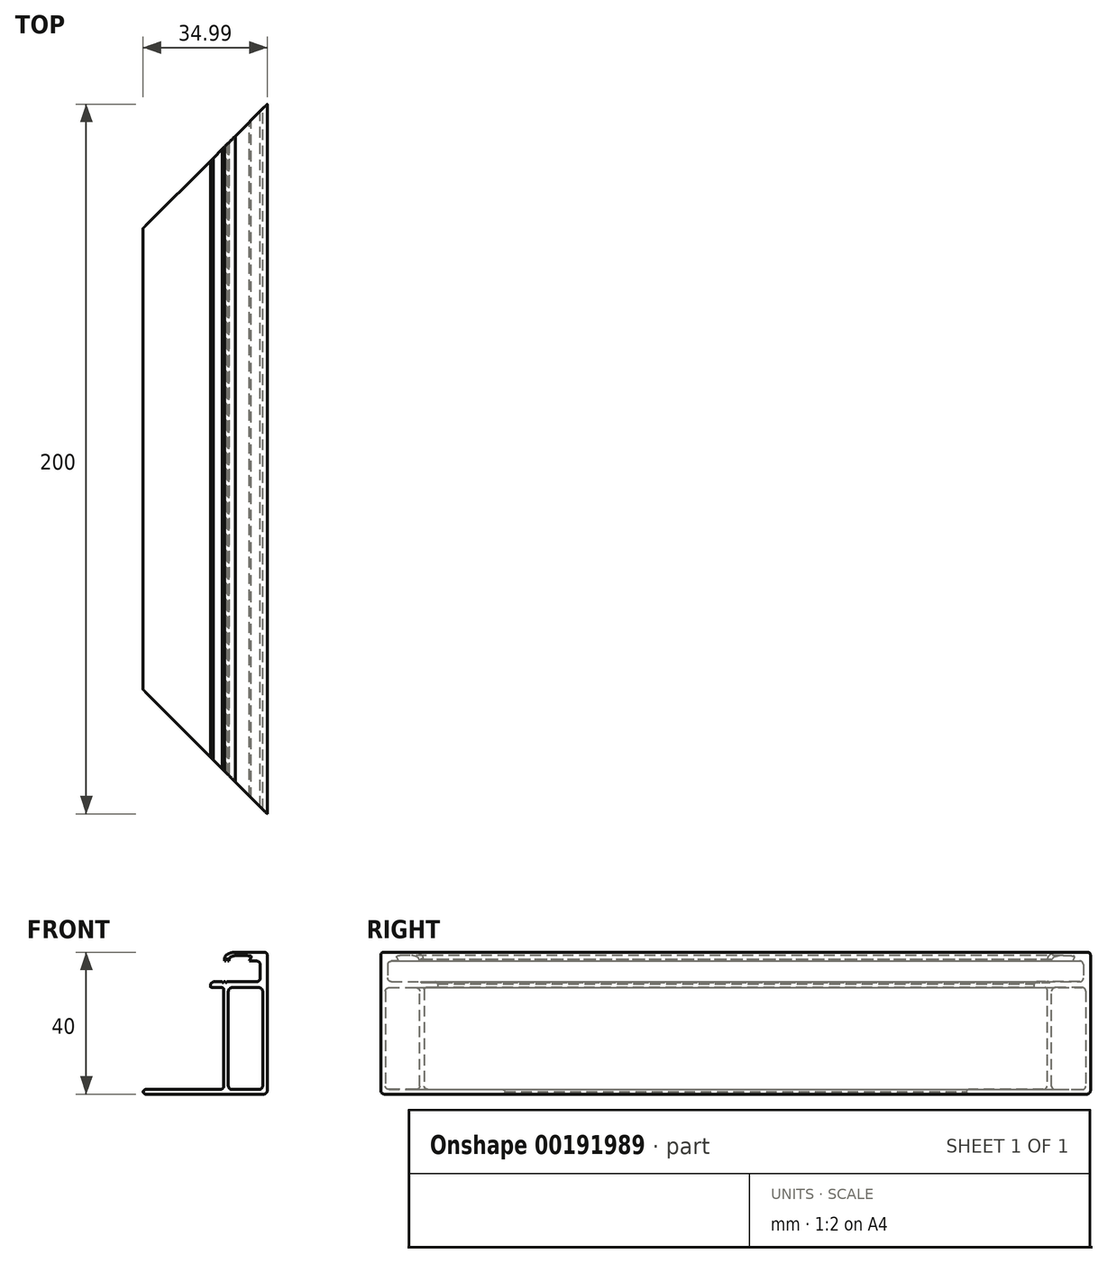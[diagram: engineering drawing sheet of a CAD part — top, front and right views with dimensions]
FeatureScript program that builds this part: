
annotation { "Feature Type Name" : "Feature", "Feature Type Description" : "" }
export const myFeature = defineFeature(function(context is Context, id is Id, definition is map)
    precondition{}
    {
        {
            var Q0;
            Q0=qCreatedBy(makeId("Front.planeOp"),FACE);
            var sketch = newSketch(context, id + "F0", { "sketchPlane" : qUnion([Q0])});
            skLineSegment(sketch, "E0", {"start": v(23, 40) * mm, "end": v(23, 37.5) * mm});
            skLineSegment(sketch, "E1", {"start": v(23, 37.5) * mm, "end": v(33, 37.5) * mm});
            skLineSegment(sketch, "E2", {"start": v(33, 37.5) * mm, "end": v(33, 31.7) * mm});
            skLineSegment(sketch, "E3", {"start": v(33, 31.7) * mm, "end": v(19, 31.7) * mm});
            skLineSegment(sketch, "E4", {"start": v(19, 31.7) * mm, "end": v(19, 30) * mm});
            skLineSegment(sketch, "E5", {"start": v(19, 30) * mm, "end": v(22.74, 30) * mm});
            skLineSegment(sketch, "E6", {"start": v(22.74, 30) * mm, "end": v(22.74, 1.3) * mm});
            skLineSegment(sketch, "E7", {"start": v(22.74, 1.3) * mm, "end": v(0, 1.3) * mm});
            skLineSegment(sketch, "E8", {"start": v(0, 1.3) * mm, "end": v(0, 0) * mm});
            skLineSegment(sketch, "E9", {"start": v(33.7, 30) * mm, "end": v(33.7, 1.3) * mm});
            skLineSegment(sketch, "E10", {"start": v(24.04, 1.3) * mm, "end": v(33.7, 1.3) * mm});
            skLineSegment(sketch, "E11", {"start": v(24.04, 1.3) * mm, "end": v(24.04, 30) * mm});
            skLineSegment(sketch, "E12", {"start": v(33.7, 30) * mm, "end": v(24.04, 30) * mm});
            skLineSegment(sketch, "E13", {"start": v(23, 40) * mm, "end": v(35, 40) * mm});
            skLineSegment(sketch, "E14", {"start": v(35, 40) * mm, "end": v(35, 0) * mm});
            skLineSegment(sketch, "E15", {"start": v(35, 0) * mm, "end": v(0, 0) * mm});
            skLineSegment(sketch, "E16", {"start": v(19, 31.08) * mm, "end": v(19.79, 31.7) * mm});
            skCircle(sketch, "E17", {"center": v(19.14, 30) * mm, "radius": 0.15 * mm});
            skLineSegment(sketch, "E18", {"start": v(22.36, 31.7) * mm, "end": v(22.36, 31.5) * mm});
            skLineSegment(sketch, "E19", {"start": v(22.36, 31.5) * mm, "end": v(22.76, 31.5) * mm});
            skLineSegment(sketch, "E20", {"start": v(22.76, 31.5) * mm, "end": v(22.76, 31.7) * mm});
            skLineSegment(sketch, "E21", {"start": v(23.2, 31.7) * mm, "end": v(23.2, 31.5) * mm});
            skLineSegment(sketch, "E22", {"start": v(23.2, 31.5) * mm, "end": v(23.6, 31.5) * mm});
            skLineSegment(sketch, "E23", {"start": v(23.6, 31.5) * mm, "end": v(23.6, 31.7) * mm});
            skFitSpline(sketch, "E24", {"points": [v(23, 38.13) * mm, v(26.36, 40) * mm], "startDerivative": vector(-0.03, 4.16) * mm, "endDerivative": vector(4.34, -0.14) * mm});
            skLineSegment(sketch, "E25", {"start": v(23.36, 37.5) * mm, "end": v(23.36, 38) * mm});
            skLineSegment(sketch, "E26", {"start": v(23.36, 38) * mm, "end": v(23.85, 38) * mm});
            skLineSegment(sketch, "E27", {"start": v(23.85, 38) * mm, "end": v(23.85, 37.5) * mm});
            skLineSegment(sketch, "E28", {"start": v(23.85, 37.5) * mm, "end": v(24.2, 37.5) * mm});
            skFitSpline(sketch, "E29", {"points": [v(24.2, 37.5) * mm, v(30.68, 39) * mm], "startDerivative": vector(-1.37, 7.17) * mm, "endDerivative": vector(3.82, 0.47) * mm});
            skLineSegment(sketch, "E30", {"start": v(30.68, 39) * mm, "end": v(30, 37.5) * mm});
            skArc(sketch, "E31", {"start": v(23.36, 37.5) * mm, "mid": v(23.18, 37.32) * mm, "end": v(23, 37.5) * mm});
            skArc(sketch, "E32", {"start": v(23.85, 37.5) * mm, "mid": v(24.02, 37.32) * mm, "end": v(24.2, 37.5) * mm});
            skSolve(sketch);
        }
        {
            var Q0;
            {var subQ15=sQuery(id+"F0.wireOp",EDGE,"E2");Q0=makeQuery(id+"F0.imprint","IMPRINT",FACE,{"disambiguationData":[TD([[makeQuery(id+"F0.imprint","IMPRINT",EDGE,{"derivedFrom":subQ15}),1.0]])]});}
            var Q1;
            {var subQ0=sQuery(id+"F0.wireOp",EDGE,"E31");Q1=makeQuery(id+"F0.imprint","IMPRINT",FACE,{"disambiguationData":[TD([[makeQuery(id+"F0.imprint","IMPRINT",EDGE,{"derivedFrom":subQ0}),-1.0]])]});}
            var Q2;
            Q2=makeQuery(id+"F0.imprint","IMPRINT",FACE,{"disambiguationData":[TD([[makeQuery(id+"F0.imprint","IMPRINT",EDGE,{"derivedFrom":sQuery(id+"F0.wireOp",EDGE,"E28")}),-1.0]])]});
            extrude(context, id + "F1", {"entities" : qUnion([Q0, Q1, Q2]), "depth" : 200 * mm});
        }
        {
            var Q0;
            Q0=makeQuery(id+"F1.opExtrude","SWEPT_FACE",FACE,{"disambiguationData":[OSD([sQuery(id+"F0.wireOp",EDGE,"E15")])]});
            var sketch = newSketch(context, id + "F2", { "sketchPlane" : qUnion([Q0])});
            skLineSegment(sketch, "E33", {"start": v(35, 200) * mm, "end": v(0, 165) * mm});
            skLineSegment(sketch, "E34", {"start": v(35, 0) * mm, "end": v(0, 35) * mm});
            skSolve(sketch);
        }
        {
            var Q0;
            Q0=makeQuery(id+"F1.opExtrude","SWEPT_EDGE",EDGE,{"disambiguationData":[OSD([sQuery(id+"F0.wireOp",EDGE,"E9"),sQuery(id+"F0.wireOp",EDGE,"E12")])]});
            var Q1;
            Q1=makeQuery(id+"F1.opExtrude","SWEPT_EDGE",EDGE,{"disambiguationData":[OSD([sQuery(id+"F0.wireOp",EDGE,"E9"),sQuery(id+"F0.wireOp",EDGE,"E10")])]});
            var Q2;
            Q2=makeQuery(id+"F1.opExtrude","SWEPT_EDGE",EDGE,{"disambiguationData":[OSD([sQuery(id+"F0.wireOp",EDGE,"E10"),sQuery(id+"F0.wireOp",EDGE,"E11")])]});
            var Q3;
            Q3=makeQuery(id+"F1.opExtrude","SWEPT_EDGE",EDGE,{"disambiguationData":[OSD([sQuery(id+"F0.wireOp",EDGE,"E11"),sQuery(id+"F0.wireOp",EDGE,"E12")])]});
            fillet(context, id + "F3", {"entities" : qUnion([Q0, Q1, Q2, Q3]), "radius" : 1 * mm, "tangentPropagation" : true, "allowEdgeOverflow" : false});
        }
        {
            var Q0;
            Q0=makeQuery(id+"F1.opExtrude","SWEPT_EDGE",EDGE,{"disambiguationData":[OSD([sQuery(id+"F0.wireOp",EDGE,"E6"),sQuery(id+"F0.wireOp",EDGE,"E7")])]});
            fillet(context, id + "F4", {"entities" : qUnion([Q0]), "radius" : 1 * mm, "tangentPropagation" : true, "allowEdgeOverflow" : false});
        }
        {
            var Q0;
            Q0=makeQuery(id+"F1.opExtrude","SWEPT_EDGE",EDGE,{"disambiguationData":[OSD([sQuery(id+"F0.wireOp",EDGE,"E2"),sQuery(id+"F0.wireOp",EDGE,"E3")])]});
            var Q1;
            Q1=makeQuery(id+"F1.opExtrude","SWEPT_EDGE",EDGE,{"disambiguationData":[OSD([sQuery(id+"F0.wireOp",EDGE,"E1"),sQuery(id+"F0.wireOp",EDGE,"E2")])]});
            fillet(context, id + "F5", {"entities" : qUnion([Q0, Q1]), "radius" : 1 * mm, "tangentPropagation" : true, "allowEdgeOverflow" : false});
        }
        {
            var Q0;
            Q0=makeQuery(id+"F1.opExtrude","SWEPT_EDGE",EDGE,{"disambiguationData":[OSD([sQuery(id+"F0.wireOp",EDGE,"E29"),sQuery(id+"F0.wireOp",EDGE,"E30")])]});
            fillet(context, id + "F6", {"entities" : qUnion([Q0]), "radius" : .3 * mm, "tangentPropagation" : true, "allowEdgeOverflow" : false});
        }
        {
            var Q0;
            Q0=makeQuery(id+"F1.opExtrude","SWEPT_EDGE",EDGE,{"disambiguationData":[OSD([sQuery(id+"F0.wireOp",EDGE,"E7"),sQuery(id+"F0.wireOp",EDGE,"E8")])]});
            var Q1;
            Q1=makeQuery(id+"F1.opExtrude","SWEPT_EDGE",EDGE,{"disambiguationData":[OSD([sQuery(id+"F0.wireOp",EDGE,"E8"),sQuery(id+"F0.wireOp",EDGE,"E15")])]});
            fillet(context, id + "F7", {"entities" : qUnion([Q0, Q1]), "radius" : .8 * mm, "tangentPropagation" : true, "allowEdgeOverflow" : false});
        }
        {
            var Q0;
            Q0=makeQuery(id+"F1.opExtrude","SWEPT_EDGE",EDGE,{"disambiguationData":[OSD([sQuery(id+"F0.wireOp",EDGE,"E14"),sQuery(id+"F0.wireOp",EDGE,"E15")])]});
            fillet(context, id + "F8", {"entities" : qUnion([Q0]), "radius" : 1 * mm, "tangentPropagation" : true, "allowEdgeOverflow" : false});
        }
        {
            var Q0;
            Q0=makeQuery(id+"F1.opExtrude","SWEPT_EDGE",EDGE,{"disambiguationData":[OSD([sQuery(id+"F0.wireOp",EDGE,"E13"),sQuery(id+"F0.wireOp",EDGE,"E14")])]});
            fillet(context, id + "F9", {"entities" : qUnion([Q0]), "radius" : .8 * mm, "tangentPropagation" : true, "allowEdgeOverflow" : false});
        }
        {
            var Q0;
            Q0=makeQuery(id+"F1.opExtrude","SWEPT_EDGE",EDGE,{"disambiguationData":[OSD([sQuery(id+"F0.wireOp",EDGE,"E5"),sQuery(id+"F0.wireOp",EDGE,"E6")])]});
            fillet(context, id + "F10", {"entities" : qUnion([Q0]), "radius" : .5 * mm, "tangentPropagation" : true, "allowEdgeOverflow" : false});
        }
        {
            var Q0;
            {var subQ0=sQuery(id+"F2.wireOp",EDGE,"E33");Q0=makeQuery(id+"F2.imprint","IMPRINT",FACE,{"disambiguationData":[TD([[makeQuery(id+"F2.imprint","IMPRINT",EDGE,{"derivedFrom":subQ0}),-1.0]])]});}
            var Q1;
            {var subQ0=sQuery(id+"F2.wireOp",EDGE,"E34");Q1=makeQuery(id+"F2.imprint","IMPRINT",FACE,{"disambiguationData":[TD([[makeQuery(id+"F2.imprint","IMPRINT",EDGE,{"derivedFrom":subQ0}),1.0]])]});}
            extrude(context, id + "F11", {"entities" : qUnion([Q0, Q1]), "operationType" : NewBodyOperationType.REMOVE, "endBound" : BoundingType.THROUGH_ALL, "oppositeDirection" : true, "depth" : 25.4 * mm});
        }
    });
